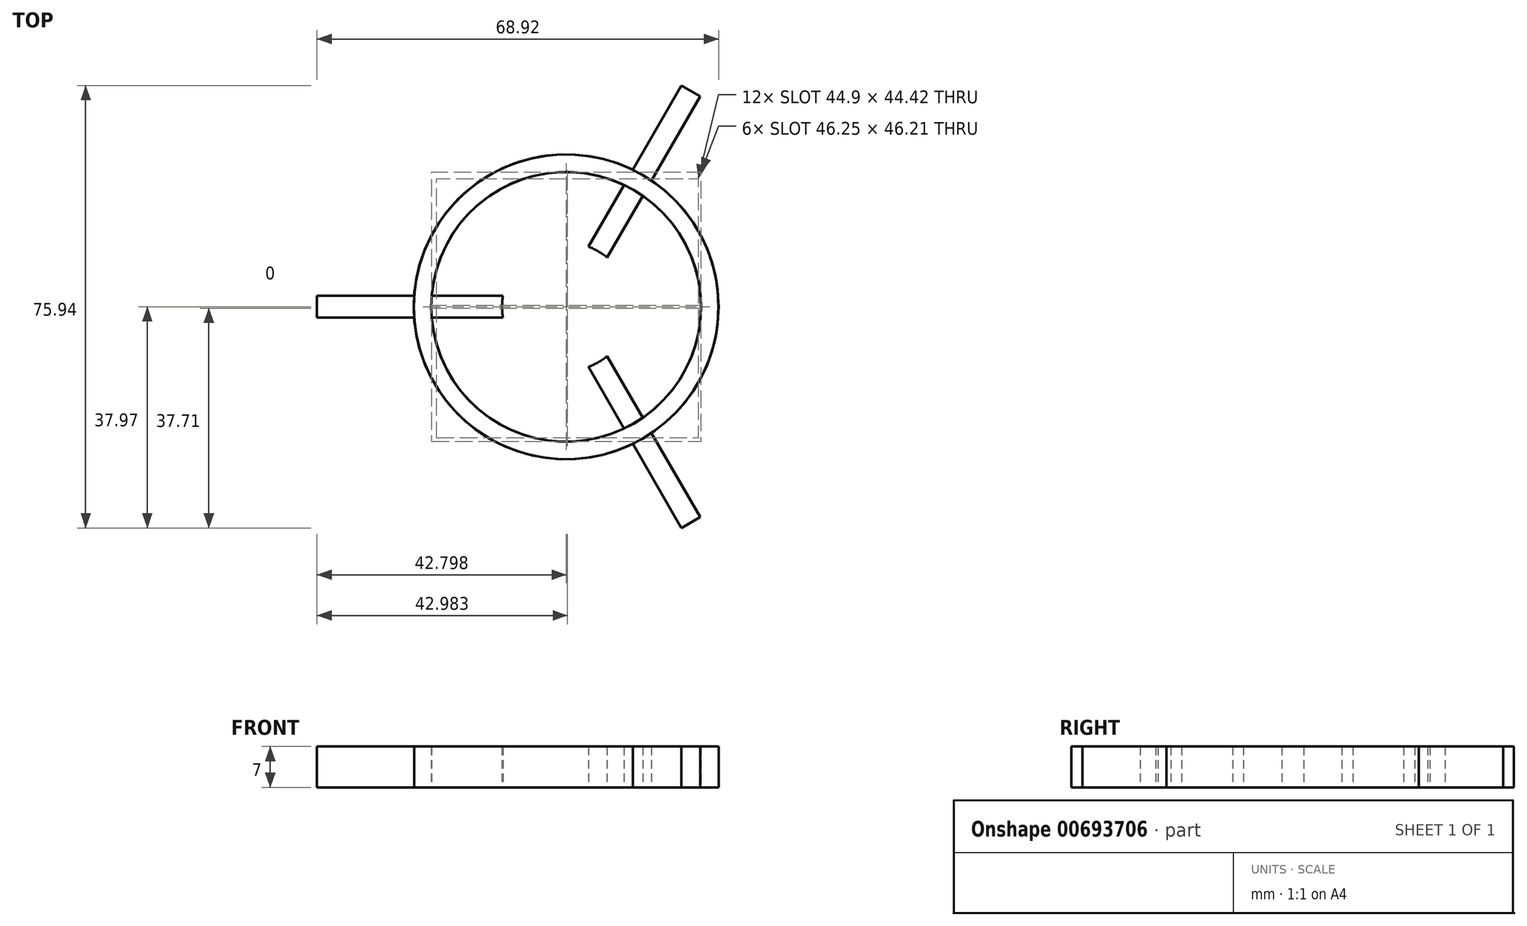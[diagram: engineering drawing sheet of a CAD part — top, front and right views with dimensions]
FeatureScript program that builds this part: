
annotation { "Feature Type Name" : "Feature", "Feature Type Description" : "" }
export const myFeature = defineFeature(function(context is Context, id is Id, definition is map)
    precondition{}
    {
        {
            var Q0;
            Q0=qCreatedBy(makeId("Top.planeOp"),FACE);
            var sketch = newSketch(context, id + "F0", { "sketchPlane" : qUnion([Q0])});
            skArc(sketch, "E0", {"start": v(-10.84, 1.87) * mm, "mid": v(-11, 0) * mm, "end": v(-10.84, -1.87) * mm});
            skLineSegment(sketch, "E1.bottom", {"start": v(-10.84, -1.87) * mm, "end": v(-23.07, -1.87) * mm});
            skLineSegment(sketch, "E1.top", {"start": v(-10.84, 1.87) * mm, "end": v(-23.07, 1.87) * mm});
            skLineSegment(sketch, "E1.right", {"start": v(-42.76, -1.87) * mm, "end": v(-42.76, 1.87) * mm});
            skPoint(sketch, "E1.middle", {"position": v(-24.82, 0) * mm});
            skPoint(sketch, "E1.left.start.orphan", {"position": v(-6.88, -1.87) * mm});
            skPoint(sketch, "E2.orphan", {"position": v(-6.88, 1.87) * mm});
            skArc(sketch, "E3", {"start": v(-23.07, -1.87) * mm, "mid": v(23.14, 0) * mm, "end": v(-23.07, 1.87) * mm});
            skArc(sketch, "E4", {"start": v(-26.09, -1.87) * mm, "mid": v(26.16, 0) * mm, "end": v(-26.09, 1.87) * mm});
            skLineSegment(sketch, "E5.trimOffspring", {"start": v(-26.09, 1.87) * mm, "end": v(-42.76, 1.87) * mm});
            skLineSegment(sketch, "E6.trimOffspring", {"start": v(-26.09, -1.87) * mm, "end": v(-42.76, -1.87) * mm});
            skSolve(sketch);
        }
        {
            var Q0;
            Q0=makeQuery(id+"F0.imprint","IMPRINT",FACE,{"disambiguationData":[TD([[makeQuery(id+"F0.imprint","IMPRINT",EDGE,{"derivedFrom":sQuery(id+"F0.wireOp",EDGE,"E0")}),-1.0]])]});
            extrude(context, id + "F1", {"entities" : qUnion([Q0]), "depth" : 7 * mm, "offsetDistance" : 25.4 * mm});
        }
        {
            var Q0;
            Q0=makeQuery(id+"F1.opExtrude","SWEPT_BODY",BODY,{"disambiguationData":[OSD([sQuery(id+"F0.wireOp",EDGE,"E0"),sQuery(id+"F0.wireOp",EDGE,"E1.bottom"),sQuery(id+"F0.wireOp",EDGE,"E1.top"),sQuery(id+"F0.wireOp",EDGE,"E1.right"),sQuery(id+"F0.wireOp",EDGE,"E3"),sQuery(id+"F0.wireOp",EDGE,"E4"),sQuery(id+"F0.wireOp",EDGE,"E5.trimOffspring"),sQuery(id+"F0.wireOp",EDGE,"E6.trimOffspring")])]});
            var Q1;
            Q1=makeQuery(id+"F1.opExtrude","SWEPT_FACE",FACE,{"disambiguationData":[OSD([sQuery(id+"F0.wireOp",EDGE,"E0")])]});
            circularPattern(context, id + "F2", {"entities" : qUnion([Q0]), "axis" : qUnion([Q1]), "angle" : 360 * degree, "instanceCount" : 3, "equalSpace" : true});
        }
    });
